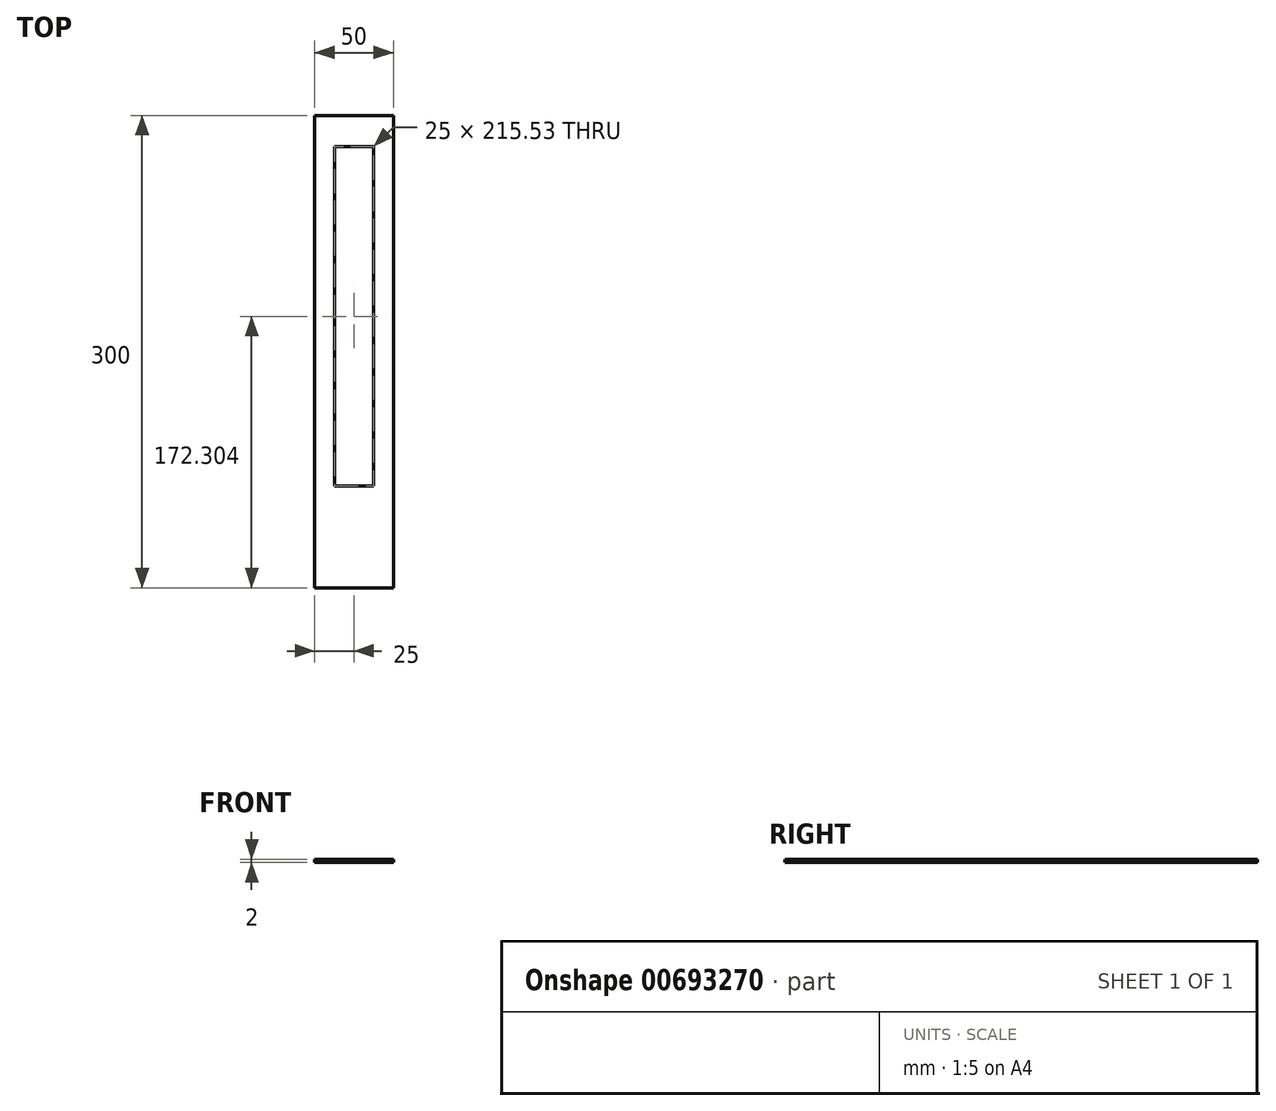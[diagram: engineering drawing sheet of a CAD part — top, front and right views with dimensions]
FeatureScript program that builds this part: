
annotation { "Feature Type Name" : "Feature", "Feature Type Description" : "" }
export const myFeature = defineFeature(function(context is Context, id is Id, definition is map)
    precondition{}
    {
        {
            var Q0;
            Q0=qCreatedBy(makeId("Top.planeOp"),FACE);
            var sketch = newSketch(context, id + "F0", { "sketchPlane" : qUnion([Q0])});
            skLineSegment(sketch, "E0.bottom", {"start": v(-17.24, -64.54) * mm, "end": v(32.76, -64.54) * mm});
            skLineSegment(sketch, "E0.top", {"start": v(-17.24, 235.46) * mm, "end": v(32.76, 235.46) * mm});
            skLineSegment(sketch, "E0.left", {"start": v(-17.24, -64.54) * mm, "end": v(-17.24, 235.46) * mm});
            skLineSegment(sketch, "E0.right", {"start": v(32.76, -64.54) * mm, "end": v(32.76, 235.46) * mm});
            skLineSegment(sketch, "E1", {"start": v(7.76, 235.46) * mm, "end": v(7.76, -64.54) * mm, "construction": true});
            skLineSegment(sketch, "E2", {"start": v(7.76, -64.54) * mm, "end": v(7.76, 235.46) * mm, "construction": true});
            skLineSegment(sketch, "E3", {"start": v(-17.24, 235.46) * mm, "end": v(7.76, 235.46) * mm, "construction": true});
            skLineSegment(sketch, "E4", {"start": v(32.76, 235.46) * mm, "end": v(7.76, 235.46) * mm, "construction": true});
            skLineSegment(sketch, "E5", {"start": v(32.76, -64.54) * mm, "end": v(7.76, -64.54) * mm, "construction": true});
            skLineSegment(sketch, "E6", {"start": v(-17.24, -64.54) * mm, "end": v(7.76, -64.54) * mm, "construction": true});
            skLineSegment(sketch, "E7", {"start": v(-17.24, -64.54) * mm, "end": v(-17.24, 0) * mm, "construction": true});
            skLineSegment(sketch, "E8", {"start": v(-17.24, 235.46) * mm, "end": v(-17.24, 215.46) * mm, "construction": true});
            skLineSegment(sketch, "E9", {"start": v(-4.74, 215.53) * mm, "end": v(-4.74, 0) * mm});
            skPoint(sketch, "E9.startSnap0", {"position": v(-4.74, 235.46) * mm});
            skLineSegment(sketch, "E10", {"start": v(-4.74, 0) * mm, "end": v(20.26, 0) * mm});
            skPoint(sketch, "E10.endSnap0", {"position": v(20.26, 235.46) * mm});
            skLineSegment(sketch, "E11", {"start": v(20.26, 0) * mm, "end": v(20.26, 215.53) * mm});
            skLineSegment(sketch, "E12", {"start": v(20.26, 215.53) * mm, "end": v(-4.74, 215.53) * mm});
            skSolve(sketch);
        }
        {
            var Q0;
            Q0 = qSketchRegion(id + "F0", true);
            extrude(context, id + "F1", {"entities" : qUnion([Q0]), "depth" : 2 * mm, "offsetDistance" : 25 * mm});
        }
    });
